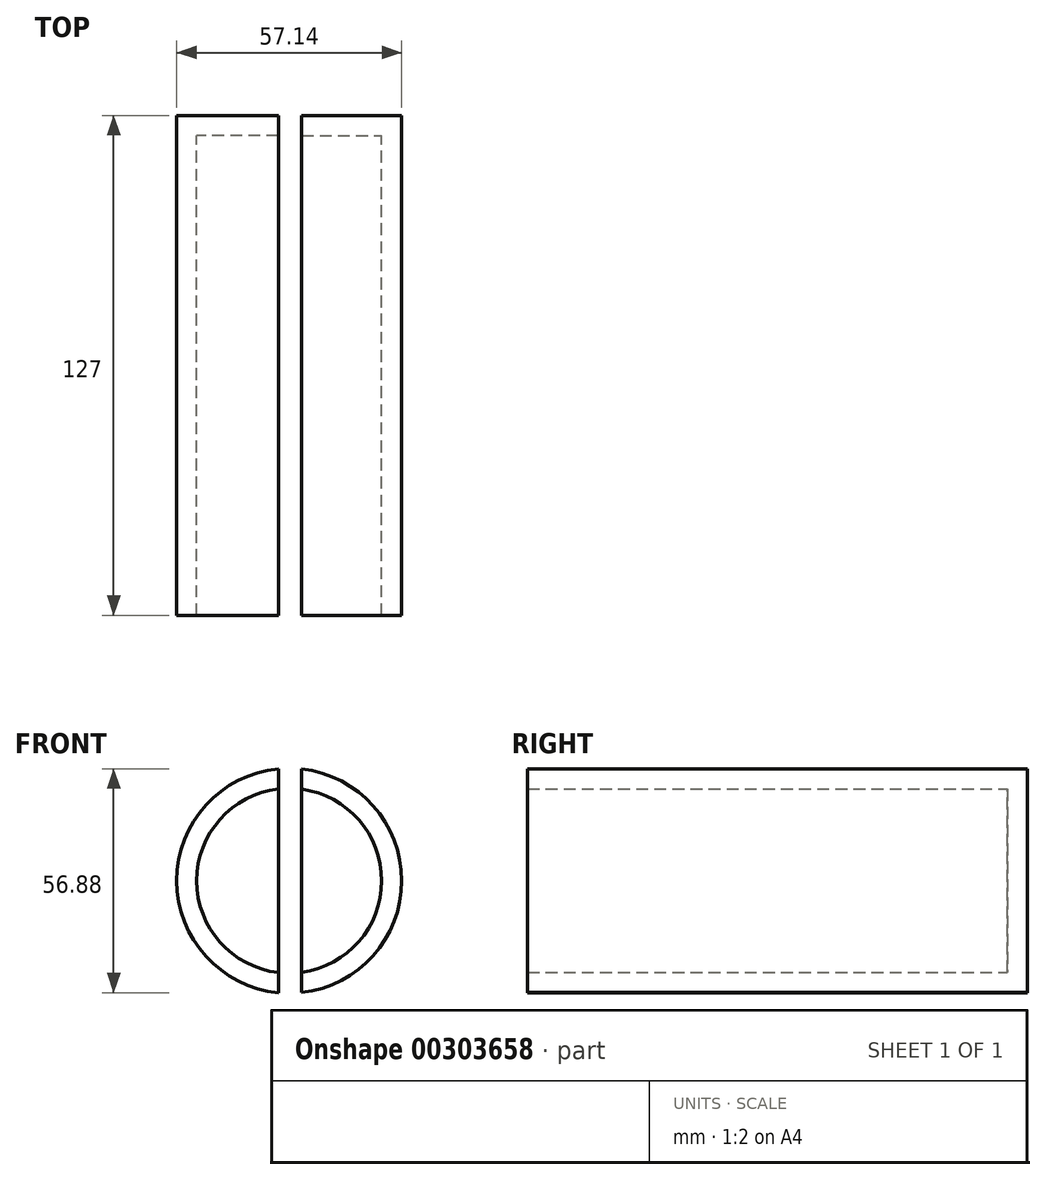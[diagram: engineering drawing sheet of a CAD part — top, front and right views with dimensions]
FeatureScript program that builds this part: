
annotation { "Feature Type Name" : "Feature", "Feature Type Description" : "" }
export const myFeature = defineFeature(function(context is Context, id is Id, definition is map)
    precondition{}
    {
        {
            var Q0;
            Q0=qCreatedBy(makeId("Front.planeOp"),FACE);
            var sketch = newSketch(context, id + "F0", { "sketchPlane" : qUnion([Q0])});
            skCircle(sketch, "E0", {"center": v(0, 0) * mm, "radius": 28.58 * mm});
            skSolve(sketch);
        }
        {
            var Q0;
            Q0=makeQuery(id+"F0.imprint","IMPRINT",FACE,{"disambiguationData":[TD([[makeQuery(id+"F0.imprint","IMPRINT",EDGE,{"derivedFrom":sQuery(id+"F0.wireOp",EDGE,"E0")}),1.0]])]});
            extrude(context, id + "F1", {"entities" : qUnion([Q0]), "depth" : 127 * mm});
        }
        {
            var Q0;
            Q0=makeQuery(id+"F1.opExtrude","CAP_FACE",FACE,{"disambiguationData":[OSD([sQuery(id+"F0.wireOp",EDGE,"E0")])],"isStart":false});
            shell(context, id + "F2", {"entities" : qUnion([Q0]), "thickness" : 5.08 * mm});
        }
        {
            var Q0;
            Q0=qCreatedBy(makeId("Front.planeOp"),FACE);
            var sketch = newSketch(context, id + "F3", { "sketchPlane" : qUnion([Q0])});
            skLineSegment(sketch, "E1", {"start": v(0, 59) * mm, "end": v(0, -54.68) * mm});
            skLineSegment(sketch, "E2", {"start": v(0, 59) * mm, "end": v(-2.75, 59) * mm});
            skLineSegment(sketch, "E3", {"start": v(-2.75, 59) * mm, "end": v(-2.75, -54.49) * mm});
            skLineSegment(sketch, "E4", {"start": v(-2.75, -54.49) * mm, "end": v(0, -54.68) * mm});
            skLineSegment(sketch, "E5", {"start": v(3.2, -54.68) * mm, "end": v(3.2, 59) * mm});
            skLineSegment(sketch, "E6", {"start": v(3.2, 59) * mm, "end": v(0, 59) * mm});
            skLineSegment(sketch, "E7", {"start": v(3.2, -54.68) * mm, "end": v(0, -54.68) * mm});
            skSolve(sketch);
        }
        {
            var Q0;
            Q0 = qSketchRegion(id + "F3", true);
            extrude(context, id + "F4", {"entities" : qUnion([Q0]), "operationType" : NewBodyOperationType.REMOVE, "depth" : 609.6 * mm});
        }
    });
